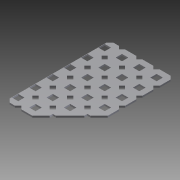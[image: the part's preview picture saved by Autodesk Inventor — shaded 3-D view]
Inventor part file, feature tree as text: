
AUTODESK INVENTOR PART (.ipt)
format: ipt  version: 2012 (Build 160160000, 160)  size: 693,760 bytes
history: native  units: in
note: dims shown in document units (in); Inventor stores cm internally (conversion verified against a paired STEP export)
features: plane x4, split x3, other x2, chamfer x2, imported_body x1, extrude x1, sketch x1
ambient origin geometry x8: Origin, YZ Plane, XZ Plane, XY Plane, X Axis, Y Axis, Z Axis, Center Point
feature tree (14):
  parser-record x1  (decoder bookkeeping rows leaked as tree rows — omitted from the tree; the rows remain in map.json)
  imported_body  "Base1"
  plane  "Work Plane1"
  split  "Split1"
  plane  "Work Plane2"
  split  "Split2"
  extrude  "Extrusion1"  [1 undecoded]
  plane  "Work Plane3"
  split  "Split3"
  chamfer  "Chamfer1"  Distance=1.0in
  chamfer  "Chamfer2"  [1 undecoded]
  other  "Alias Freeform1"
  plane  "Work Plane4"
  sketch  "Sketch1"  dims[d0=-0.5in d1=-3.0in d2=1.0in d3=0.0in d4=-0.15in d5=0.07in d6=0.125in d7=45.0deg d8=0.07in d9=0.125in d10=45.0deg d11=-0.03in]
note: 2 required parameter values undecoded (feature->parameter linkage not recoverable at this tier; creation-order binding heuristic only, values carry confidence <= 0.55)
